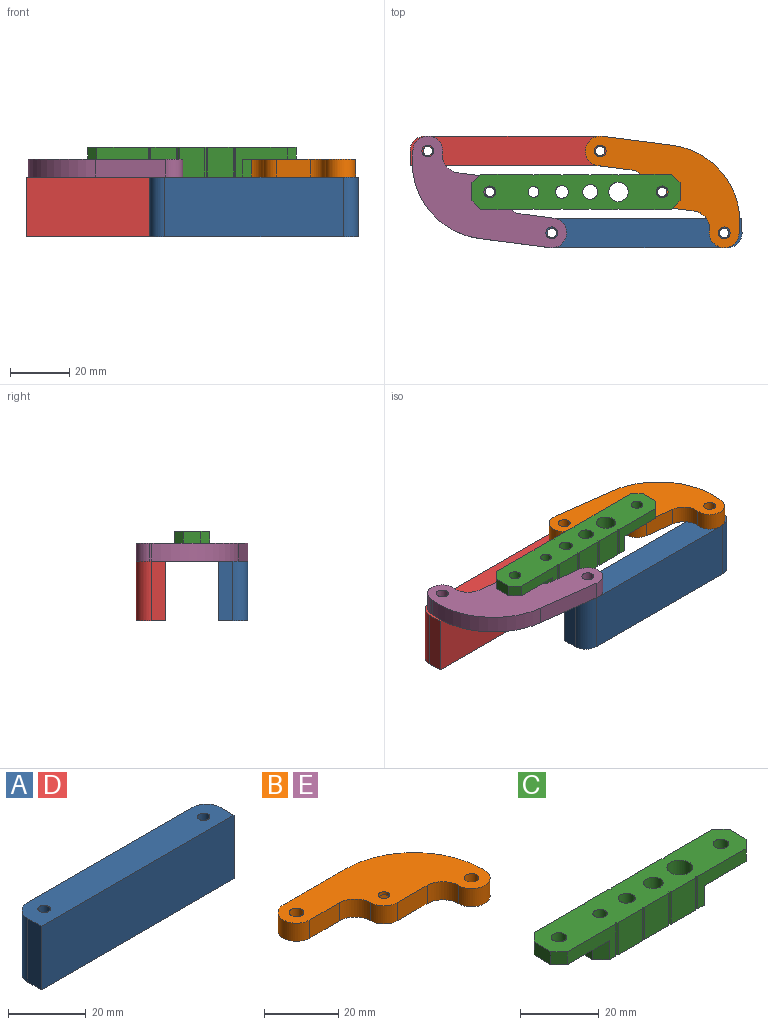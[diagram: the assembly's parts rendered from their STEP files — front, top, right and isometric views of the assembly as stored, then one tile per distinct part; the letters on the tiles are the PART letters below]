
ASSEMBLY  parts=5 mates=10
PART A: 10 faces, bbox 70x10x20 mm
  f0: plane 70x20mm, normal (0,-1,0), area 1400mm2, adj f1,f5,f6,f7
  f1: plane 20x5mm, normal (1,0,0), area 100mm2, adj f0,f6,f7,f8
  f2: plane 60x20mm, normal (0,1,0), area 1200mm2, adj f6,f7,f8,f9
  f3: cylinder r=1.6mm len=20mm, axis (0,0,-1), area 201.1mm2, adj f6,f7
  f4: cylinder r=1.6mm len=20mm, axis (0,0,-1), area 201.1mm2, adj f6,f7
  f5: plane 20x5mm, normal (-1,0,0), area 100mm2, adj f0,f6,f7,f9
  f6: plane 70x10mm, normal (0,0,1), area 673.2mm2, adj f0,f1,f2,f3,f4,f5,f8,f9
  f7: plane 70x10mm, normal (0,0,-1), area 673.2mm2, adj f0,f1,f2,f3,f4,f5,f8,f9
  f8: cylinder r=5mm len=20mm, axis (0,0,-1), area 157.1mm2, adj f1,f2,f6,f7
  f9: cylinder r=5mm len=20mm, axis (0,0,1), area 157.1mm2, adj f2,f5,f6,f7
PART B: 22 faces, bbox 54.9x32x6 mm
  f0: cylinder r=1.6mm len=3.2mm, axis (0,0,-1), area 10.1mm2, adj f14,f21
  f1: plane 54.9x32mm, normal (0,0,-1), area 791.4mm2, adj f2,f3,f4,f5,f6,f7,f8,f9
  f2: cylinder r=5mm len=10mm, axis (0,0,-1), area 94.2mm2, adj f1,f3,f13,f14
  f3: plane 6x0.95mm, normal (1,0,0), area 5.7mm2, adj f1,f2,f4,f14
  f4: cylinder r=26.05mm len=26.05mm, axis (0,0,-1), area 245.5mm2, adj f1,f3,f5,f14
  f5: plane 23.85x6mm, normal (0,1,0), area 143.1mm2, adj f1,f4,f6,f14
  f6: cylinder r=5mm len=10mm, axis (0,0,-1), area 94.2mm2, adj f1,f5,f7,f14
  f7: plane 11.45x6mm, normal (0,-1,0), area 68.7mm2, adj f1,f6,f8,f14
  f8: cylinder r=6mm len=6mm, axis (0,0,-1), area 56.5mm2, adj f1,f7,f9,f14
  f9: cylinder r=5mm len=6mm, axis (0,0,-1), area 47.1mm2, adj f1,f8,f10,f14
  f10: plane 11.45x6mm, normal (0,-1,0), area 68.7mm2, adj f1,f9,f13,f14
  f11: cylinder r=2mm len=6mm, axis (0,0,-1), area 75.4mm2, adj f1,f14
  f12: cylinder r=2mm len=6mm, axis (0,0,-1), area 75.4mm2, adj f1,f14
  f13: cylinder r=6mm len=6mm, axis (0,0,-1), area 56.5mm2, adj f1,f2,f10,f14
  f14: plane 54.9x32mm, normal (0,0,1), area 825.8mm2, adj f0,f2,f3,f4,f5,f6,f7,f8
  f15: plane 5x4.55mm, normal (-1,0,0.09), area 21.6mm2, adj f1,f16,f20,f21
  f16: plane 5x3.94mm, normal (-0.5,0.86,0.09), area 21.6mm2, adj f1,f15,f17,f21
  f17: plane 5x3.94mm, normal (0.5,0.86,0.09), area 21.6mm2, adj f1,f16,f18,f21
  f18: plane 5x4.55mm, normal (1,0,0.09), area 21.6mm2, adj f1,f17,f19,f21
  f19: plane 5x3.94mm, normal (0.5,-0.86,0.09), area 21.6mm2, adj f1,f18,f20,f21
  f20: plane 5x3.94mm, normal (-0.5,-0.86,0.09), area 21.6mm2, adj f1,f15,f19,f21
  f21: plane 9.09x7.88mm, normal (0,0,-1), area 45.7mm2, adj f0,f15,f16,f17,f18,f19,f20
PART C: 48 faces, bbox 70x12x10 mm
  f0: plane 17.26x10mm, normal (0,1,0), area 82.6mm2, adj f6,f8,f12,f39,f41,f45
  f1: plane 6x4mm, normal (-1,0,0), area 24mm2, adj f8,f10,f39,f41
  f2: plane 17.26x10mm, normal (0,-1,0), area 82.6mm2, adj f6,f10,f13,f39,f41,f47
  f3: plane 6x4mm, normal (1,0,0), area 24mm2, adj f7,f9,f39,f43
  f4: cylinder r=2mm len=4mm, axis (0,0,-1), area 50.3mm2, adj f39,f41
  f5: cylinder r=2mm len=4mm, axis (0,0,-1), area 50.3mm2, adj f39,f43
  f6: plane 40x12mm, normal (0,0,-1), area 382.3mm2, adj f0,f2,f11,f12,f13,f14,f15,f16
  f7: plane 4x3mm, normal (0.71,0.71,0), area 17mm2, adj f3,f25,f39,f43
  f8: plane 4x3mm, normal (-0.71,0.71,0), area 17mm2, adj f0,f1,f39,f41
  f9: plane 4x3mm, normal (0.71,-0.71,0), area 17mm2, adj f3,f24,f39,f43
  f10: plane 4x3mm, normal (-0.71,-0.71,0), area 17mm2, adj f1,f2,f39,f41
  f11: plane 10x0.45mm, normal (-0.71,0.71,0), area 6.4mm2, adj f6,f12,f38,f39
  f12: plane 10x0.45mm, normal (0.71,0.71,0), area 6.4mm2, adj f0,f6,f11,f39
  f13: plane 10x0.45mm, normal (0.71,-0.71,0), area 6.4mm2, adj f2,f6,f14,f39
  f14: plane 10x0.45mm, normal (-0.71,-0.71,0), area 6.4mm2, adj f6,f13,f15,f39
  f15: plane 10x8.63mm, normal (0,-1,0), area 86.3mm2, adj f6,f14,f16,f39
  f16: plane 10x0.45mm, normal (0.71,-0.71,0), area 6.4mm2, adj f6,f15,f17,f39
  f17: plane 10x0.45mm, normal (-0.71,-0.71,0), area 6.4mm2, adj f6,f16,f18,f39
  f18: plane 10x8.63mm, normal (0,-1,0), area 86.3mm2, adj f6,f17,f19,f39
  f19: plane 10x0.45mm, normal (0.71,-0.71,0), area 6.4mm2, adj f6,f18,f20,f39
  f20: plane 10x0.45mm, normal (-0.71,-0.71,0), area 6.4mm2, adj f6,f19,f21,f39
  f21: plane 10x8.63mm, normal (0,-1,0), area 86.3mm2, adj f6,f20,f22,f39
  f22: plane 10x0.45mm, normal (0.71,-0.71,0), area 6.4mm2, adj f6,f21,f23,f39
  f23: plane 10x0.45mm, normal (-0.71,-0.71,0), area 6.4mm2, adj f6,f22,f24,f39
  f24: plane 17.26x10mm, normal (0,-1,0), area 82.6mm2, adj f6,f9,f23,f39,f43,f46
  f25: plane 17.26x10mm, normal (0,1,0), area 82.6mm2, adj f6,f7,f26,f39,f43,f44
  f26: plane 10x0.45mm, normal (-0.71,0.71,0), area 6.4mm2, adj f6,f25,f27,f39
  f27: plane 10x0.45mm, normal (0.71,0.71,0), area 6.4mm2, adj f6,f26,f28,f39
  f28: plane 10x8.63mm, normal (0,1,0), area 86.3mm2, adj f6,f27,f29,f39
  f29: plane 10x0.45mm, normal (-0.71,0.71,0), area 6.4mm2, adj f6,f28,f30,f39
  f30: plane 10x0.45mm, normal (0.71,0.71,0), area 6.4mm2, adj f6,f29,f31,f39
  f31: plane 10x8.63mm, normal (0,1,0), area 86.3mm2, adj f6,f30,f32,f39
  f32: plane 10x0.45mm, normal (-0.71,0.71,0), area 6.4mm2, adj f6,f31,f33,f39
  f33: plane 10x0.45mm, normal (0.71,0.71,0), area 6.4mm2, adj f6,f32,f38,f39
  f34: cylinder r=2.16mm len=10mm, axis (0,0,-1), area 135.7mm2, adj f6,f39
  f35: cylinder r=3.26mm len=10mm, axis (0,0,-1), area 205.1mm2, adj f6,f39
  f36: cylinder r=1.83mm len=10mm, axis (0,0,-1), area 114.9mm2, adj f6,f39
  f37: cylinder r=2.49mm len=10mm, axis (0,0,-1), area 156.4mm2, adj f6,f39
  f38: plane 10x8.63mm, normal (0,1,0), area 86.3mm2, adj f6,f11,f33,f39
  f39: plane 70x12mm, normal (0,0,1), area 717.2mm2, adj f0,f1,f2,f3,f4,f5,f7,f8
  f40: plane 6x6mm, normal (-1,0,0), area 36mm2, adj f6,f41,f45,f47
  f41: plane 18x12mm, normal (0,0,-1), area 167.4mm2, adj f0,f1,f2,f4,f8,f10,f40,f45
  f42: plane 6x6mm, normal (1,0,0), area 36mm2, adj f6,f43,f44,f46
  f43: plane 18x12mm, normal (0,0,-1), area 167.4mm2, adj f3,f5,f7,f9,f24,f25,f42,f44
  f44: plane 6x3mm, normal (0.71,0.71,0), area 25.5mm2, adj f6,f25,f42,f43
  f45: plane 6x3mm, normal (-0.71,0.71,0), area 25.5mm2, adj f0,f6,f40,f41
  f46: plane 6x3mm, normal (0.71,-0.71,0), area 25.5mm2, adj f6,f24,f42,f43
  f47: plane 6x3mm, normal (-0.71,-0.71,0), area 25.5mm2, adj f2,f6,f40,f41
PART D: same geometry as A
PART E: same geometry as B
PLACE A rot(axis=(0,0,-1),180deg) t=(34.3,-3.53,-28.14)mm
PLACE B rot(axis=(0,0,-1),7.3deg) t=(46.72,10.25,-8.14)mm
PLACE C t=(17.72,10.25,-8.14)mm fixed
PLACE D rot(axis=(0,0,-1),0deg) t=(1.13,24.03,-28.14)mm
PLACE E rot(axis=(0,0,1),172.7deg) t=(-11.28,10.25,-8.14)mm
MATE cylindrical C.f5 <-> B.f0  axis (0,0,1) through (46.72,10.25,1.86)mm
MATE planar D.f6 <-> A.f6  axis (0,0,1) through (-3.14,23.97,-8.14)mm
MATE planar E.f1 <-> D.f6  axis (0,0,-1) through (-16.21,6.26,-8.14)mm
MATE planar C.f41 <-> E.f14  axis (0,0,-1) through (-8.87,10.25,-2.14)mm
MATE cylindrical E.f6 <-> A.f4  axis (0,0,1) through (9.58,-3.53,-2.14)mm
MATE planar E.f1 <-> B.f1  axis (0,0,-1) through (-16.21,6.26,-8.14)mm
MATE cylindrical A.f3 <-> B.f2  axis (0,0,1) through (67.58,-3.53,-8.14)mm
MATE cylindrical E.f2 <-> D.f3  axis (0,0,1) through (-32.14,24.03,-2.14)mm
MATE cylindrical E.f0 <-> C.f4  axis (0,0,1) through (-11.28,10.25,-2.14)mm
MATE cylindrical D.f4 <-> B.f6  axis (0,0,1) through (25.86,24.03,-8.14)mm
